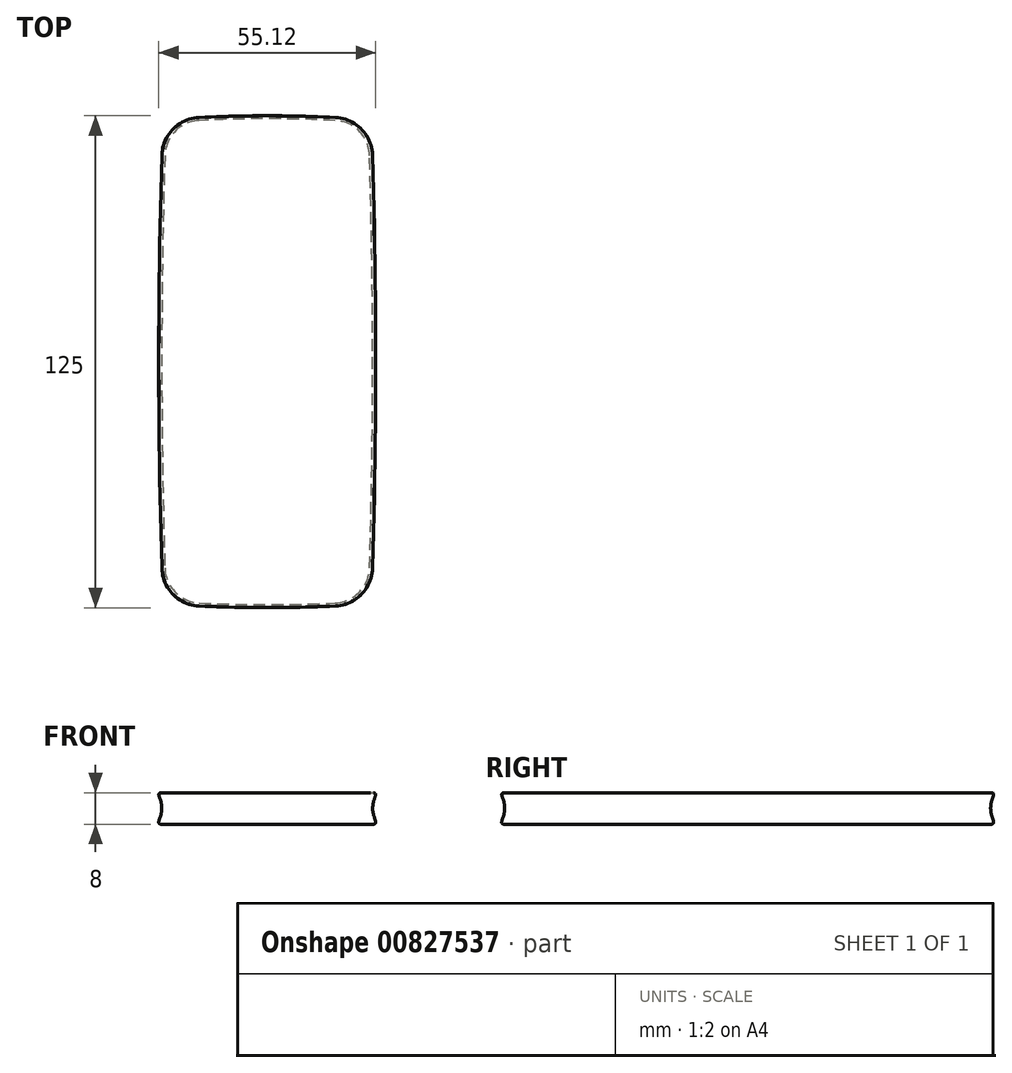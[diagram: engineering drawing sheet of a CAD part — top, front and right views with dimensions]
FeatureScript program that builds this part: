
annotation { "Feature Type Name" : "Feature", "Feature Type Description" : "" }
export const myFeature = defineFeature(function(context is Context, id is Id, definition is map)
    precondition{}
    {
        {
            var Q0;
            Q0=qCreatedBy(makeId("Top.planeOp"),FACE);
            var sketch = newSketch(context, id + "F0", { "sketchPlane" : qUnion([Q0])});
            skPoint(sketch, "E0.middle", {"position": v(0, 0) * mm});
            skArc(sketch, "E1", {"start": v(-26.53, 61.57) * mm, "mid": v(-27.35, 30.8) * mm, "end": v(-27.63, 0) * mm});
            skArc(sketch, "E2", {"start": v(0, 62.56) * mm, "mid": v(-13.28, 62.31) * mm, "end": v(-26.53, 61.57) * mm});
            skPoint(sketch, "E3.orphan", {"position": v(-27.5, 62.5) * mm});
            skArc(sketch, "E4.MirrorCS", {"start": v(-26.53, -61.57) * mm, "mid": v(-27.35, -30.8) * mm, "end": v(-27.63, 0) * mm});
            skArc(sketch, "E5.MirrorCS", {"start": v(0, -62.56) * mm, "mid": v(-13.28, -62.31) * mm, "end": v(-26.53, -61.57) * mm});
            skArc(sketch, "E6.MirrorCS", {"start": v(0, 62.56) * mm, "mid": v(13.28, 62.31) * mm, "end": v(26.53, 61.57) * mm});
            skArc(sketch, "E7.MirrorCS", {"start": v(26.53, 61.57) * mm, "mid": v(27.35, 30.8) * mm, "end": v(27.63, 0) * mm});
            skArc(sketch, "E8.MirrorCS", {"start": v(26.53, -61.57) * mm, "mid": v(27.35, -30.8) * mm, "end": v(27.63, 0) * mm});
            skArc(sketch, "E9.MirrorCS", {"start": v(0, -62.56) * mm, "mid": v(13.28, -62.31) * mm, "end": v(26.53, -61.57) * mm});
            skSolve(sketch);
        }
        {
            var Q0;
            Q0 = qSketchRegion(id + "F0", true);
            extrude(context, id + "F1", {"entities" : qUnion([Q0]), "depth" : 8 * mm, "offsetDistance" : 25 * mm});
        }
        {
            var Q0;
            Q0=makeQuery(id+"F1.opExtrude","SWEPT_EDGE",EDGE,{"disambiguationData":[OSD([sQuery(id+"F0.wireOp",EDGE,"E1"),sQuery(id+"F0.wireOp",EDGE,"E2")])]});
            var Q1;
            Q1=makeQuery(id+"F1.opExtrude","SWEPT_EDGE",EDGE,{"disambiguationData":[OSD([sQuery(id+"F0.wireOp",EDGE,"E6.MirrorCS"),sQuery(id+"F0.wireOp",EDGE,"E7.MirrorCS")])]});
            var Q2;
            Q2=makeQuery(id+"F1.opExtrude","SWEPT_EDGE",EDGE,{"disambiguationData":[OSD([sQuery(id+"F0.wireOp",EDGE,"E4.MirrorCS"),sQuery(id+"F0.wireOp",EDGE,"E5.MirrorCS")])]});
            var Q3;
            Q3=makeQuery(id+"F1.opExtrude","SWEPT_EDGE",EDGE,{"disambiguationData":[OSD([sQuery(id+"F0.wireOp",EDGE,"E8.MirrorCS"),sQuery(id+"F0.wireOp",EDGE,"E9.MirrorCS")])]});
            fillet(context, id + "F2", {"entities" : qUnion([Q0, Q1, Q2, Q3]), "radius" : 10 * mm, "tangentPropagation" : true, "allowEdgeOverflow" : false});
        }
        {
            var Q0;
            Q0=qCreatedBy(makeId("Front.planeOp"),FACE);
            var sketch = newSketch(context, id + "F3", { "sketchPlane" : qUnion([Q0])});
            skCircle(sketch, "E10", {"center": v(-33.74, 4.07) * mm, "radius": 6.95 * mm});
            skPoint(sketch, "E11.start.orphan", {"position": v(-26.8, 4.07) * mm});
            skPoint(sketch, "E12.orphan", {"position": v(-26.8, 8.13) * mm});
            skPoint(sketch, "E13.end.orphan", {"position": v(-26.8, 0) * mm});
            skSolve(sketch);
        }
        {
            var Q0;
            Q0=makeQuery(id+"F1.opExtrude","CAP_FACE",FACE,{"disambiguationData":[OSD([sQuery(id+"F0.wireOp",EDGE,"E1"),sQuery(id+"F0.wireOp",EDGE,"E2"),sQuery(id+"F0.wireOp",EDGE,"E4.MirrorCS"),sQuery(id+"F0.wireOp",EDGE,"E5.MirrorCS"),sQuery(id+"F0.wireOp",EDGE,"E6.MirrorCS"),sQuery(id+"F0.wireOp",EDGE,"E7.MirrorCS"),sQuery(id+"F0.wireOp",EDGE,"E8.MirrorCS"),sQuery(id+"F0.wireOp",EDGE,"E9.MirrorCS")])],"isStart":false});
            cPlane(context, id + "F4", {"entities" : qUnion([Q0]), "cplaneType" : CPlaneType.OFFSET, "offset" : 4 * mm, "oppositeDirection" : true, "width" : 150 * mm, "height" : 150 * mm});
        }
        {
            var Q0;
            Q0=qCreatedBy(id+"F4.planeOp",FACE);
            var sketch = newSketch(context, id + "F5", { "sketchPlane" : qUnion([Q0])});
            skArc(sketch, "E14.0", {"start": v(-25.93, -52.43) * mm, "mid": v(-23.33, -58.53) * mm, "end": v(-17.28, -61.24) * mm});
            skArc(sketch, "E14.1", {"start": v(-25.93, 52.43) * mm, "mid": v(-26.73, 0) * mm, "end": v(-25.93, -52.43) * mm});
            skArc(sketch, "E14.2", {"start": v(-17.28, -61.24) * mm, "mid": v(0, -61.66) * mm, "end": v(17.28, -61.24) * mm});
            skArc(sketch, "E14.3", {"start": v(-17.28, 61.24) * mm, "mid": v(-23.33, 58.53) * mm, "end": v(-25.93, 52.43) * mm});
            skArc(sketch, "E14.4", {"start": v(17.28, -61.24) * mm, "mid": v(23.33, -58.53) * mm, "end": v(25.93, -52.43) * mm});
            skArc(sketch, "E14.5", {"start": v(25.93, -52.43) * mm, "mid": v(26.73, 0) * mm, "end": v(25.93, 52.43) * mm});
            skArc(sketch, "E14.6", {"start": v(25.93, 52.43) * mm, "mid": v(23.33, 58.53) * mm, "end": v(17.28, 61.24) * mm});
            skArc(sketch, "E14.7", {"start": v(17.28, 61.24) * mm, "mid": v(0, 61.66) * mm, "end": v(-17.28, 61.24) * mm});
            skSolve(sketch);
        }
        {
            var Q0;
            Q0=makeQuery(id+"F3.imprint","IMPRINT",FACE,{"disambiguationData":[TD([[makeQuery(id+"F3.imprint","IMPRINT",EDGE,{"derivedFrom":sQuery(id+"F3.wireOp",EDGE,"E10")}),1.0]])]});
            var Q1;
            Q1=sQuery(id+"F5.wireOp",EDGE,"E14.1");
            var Q2;
            Q2=makeQuery(id+"F1.opExtrude","CAP_EDGE",EDGE,{"disambiguationData":[OSD([sQuery(id+"F0.wireOp",EDGE,"E1"),sQuery(id+"F0.wireOp",EDGE,"E4.MirrorCS")])],"isStart":false});
            var Q3;
            {var subQ0=sQuery(id+"F0.wireOp",EDGE,"E5.MirrorCS");var subQ1=sQuery(id+"F0.wireOp",EDGE,"E4.MirrorCS");Q3=makeQuery(id+"F2.opFillet","BLEND_EDGE",EDGE,{"blendedFrom":[makeQuery(id+"F1.opExtrude","SWEPT_EDGE",EDGE,{"disambiguationData":[OSD([subQ1,subQ0])]}),makeQuery(id+"F1.opExtrude","CAP_FACE",FACE,{"disambiguationData":[OSD([sQuery(id+"F0.wireOp",EDGE,"E1"),sQuery(id+"F0.wireOp",EDGE,"E2"),subQ1,subQ0,sQuery(id+"F0.wireOp",EDGE,"E6.MirrorCS"),sQuery(id+"F0.wireOp",EDGE,"E7.MirrorCS"),sQuery(id+"F0.wireOp",EDGE,"E8.MirrorCS"),sQuery(id+"F0.wireOp",EDGE,"E9.MirrorCS")])],"isStart":false})],"blendedInto":[makeQuery(id+"F1.opExtrude","CAP_FACE",FACE,{"disambiguationData":[OSD([sQuery(id+"F0.wireOp",EDGE,"E1"),sQuery(id+"F0.wireOp",EDGE,"E2"),subQ1,subQ0,sQuery(id+"F0.wireOp",EDGE,"E6.MirrorCS"),sQuery(id+"F0.wireOp",EDGE,"E7.MirrorCS"),sQuery(id+"F0.wireOp",EDGE,"E8.MirrorCS"),sQuery(id+"F0.wireOp",EDGE,"E9.MirrorCS")])],"isStart":false})]});}
            var Q4;
            Q4=makeQuery(id+"F1.opExtrude","CAP_EDGE",EDGE,{"disambiguationData":[OSD([sQuery(id+"F0.wireOp",EDGE,"E5.MirrorCS"),sQuery(id+"F0.wireOp",EDGE,"E9.MirrorCS")])],"isStart":false});
            var Q5;
            {var subQ0=sQuery(id+"F0.wireOp",EDGE,"E9.MirrorCS");var subQ1=sQuery(id+"F0.wireOp",EDGE,"E8.MirrorCS");Q5=makeQuery(id+"F2.opFillet","BLEND_EDGE",EDGE,{"blendedFrom":[makeQuery(id+"F1.opExtrude","SWEPT_EDGE",EDGE,{"disambiguationData":[OSD([subQ1,subQ0])]}),makeQuery(id+"F1.opExtrude","CAP_FACE",FACE,{"disambiguationData":[OSD([sQuery(id+"F0.wireOp",EDGE,"E1"),sQuery(id+"F0.wireOp",EDGE,"E2"),sQuery(id+"F0.wireOp",EDGE,"E4.MirrorCS"),sQuery(id+"F0.wireOp",EDGE,"E5.MirrorCS"),sQuery(id+"F0.wireOp",EDGE,"E6.MirrorCS"),sQuery(id+"F0.wireOp",EDGE,"E7.MirrorCS"),subQ1,subQ0])],"isStart":false})],"blendedInto":[makeQuery(id+"F1.opExtrude","CAP_FACE",FACE,{"disambiguationData":[OSD([sQuery(id+"F0.wireOp",EDGE,"E1"),sQuery(id+"F0.wireOp",EDGE,"E2"),sQuery(id+"F0.wireOp",EDGE,"E4.MirrorCS"),sQuery(id+"F0.wireOp",EDGE,"E5.MirrorCS"),sQuery(id+"F0.wireOp",EDGE,"E6.MirrorCS"),sQuery(id+"F0.wireOp",EDGE,"E7.MirrorCS"),subQ1,subQ0])],"isStart":false})]});}
            var Q6;
            Q6=makeQuery(id+"F1.opExtrude","CAP_EDGE",EDGE,{"disambiguationData":[OSD([sQuery(id+"F0.wireOp",EDGE,"E7.MirrorCS"),sQuery(id+"F0.wireOp",EDGE,"E8.MirrorCS")])],"isStart":false});
            var Q7;
            {var subQ0=sQuery(id+"F0.wireOp",EDGE,"E7.MirrorCS");var subQ1=sQuery(id+"F0.wireOp",EDGE,"E6.MirrorCS");Q7=makeQuery(id+"F2.opFillet","BLEND_EDGE",EDGE,{"blendedFrom":[makeQuery(id+"F1.opExtrude","SWEPT_EDGE",EDGE,{"disambiguationData":[OSD([subQ1,subQ0])]}),makeQuery(id+"F1.opExtrude","CAP_FACE",FACE,{"disambiguationData":[OSD([sQuery(id+"F0.wireOp",EDGE,"E1"),sQuery(id+"F0.wireOp",EDGE,"E2"),sQuery(id+"F0.wireOp",EDGE,"E4.MirrorCS"),sQuery(id+"F0.wireOp",EDGE,"E5.MirrorCS"),subQ1,subQ0,sQuery(id+"F0.wireOp",EDGE,"E8.MirrorCS"),sQuery(id+"F0.wireOp",EDGE,"E9.MirrorCS")])],"isStart":false})],"blendedInto":[makeQuery(id+"F1.opExtrude","CAP_FACE",FACE,{"disambiguationData":[OSD([sQuery(id+"F0.wireOp",EDGE,"E1"),sQuery(id+"F0.wireOp",EDGE,"E2"),sQuery(id+"F0.wireOp",EDGE,"E4.MirrorCS"),sQuery(id+"F0.wireOp",EDGE,"E5.MirrorCS"),subQ1,subQ0,sQuery(id+"F0.wireOp",EDGE,"E8.MirrorCS"),sQuery(id+"F0.wireOp",EDGE,"E9.MirrorCS")])],"isStart":false})]});}
            var Q8;
            Q8=makeQuery(id+"F1.opExtrude","CAP_EDGE",EDGE,{"disambiguationData":[OSD([sQuery(id+"F0.wireOp",EDGE,"E2"),sQuery(id+"F0.wireOp",EDGE,"E6.MirrorCS")])],"isStart":false});
            var Q9;
            {var subQ0=sQuery(id+"F0.wireOp",EDGE,"E2");var subQ1=sQuery(id+"F0.wireOp",EDGE,"E1");Q9=makeQuery(id+"F2.opFillet","BLEND_EDGE",EDGE,{"blendedFrom":[makeQuery(id+"F1.opExtrude","SWEPT_EDGE",EDGE,{"disambiguationData":[OSD([subQ1,subQ0])]}),makeQuery(id+"F1.opExtrude","CAP_FACE",FACE,{"disambiguationData":[OSD([subQ1,subQ0,sQuery(id+"F0.wireOp",EDGE,"E4.MirrorCS"),sQuery(id+"F0.wireOp",EDGE,"E5.MirrorCS"),sQuery(id+"F0.wireOp",EDGE,"E6.MirrorCS"),sQuery(id+"F0.wireOp",EDGE,"E7.MirrorCS"),sQuery(id+"F0.wireOp",EDGE,"E8.MirrorCS"),sQuery(id+"F0.wireOp",EDGE,"E9.MirrorCS")])],"isStart":false})],"blendedInto":[makeQuery(id+"F1.opExtrude","CAP_FACE",FACE,{"disambiguationData":[OSD([subQ1,subQ0,sQuery(id+"F0.wireOp",EDGE,"E4.MirrorCS"),sQuery(id+"F0.wireOp",EDGE,"E5.MirrorCS"),sQuery(id+"F0.wireOp",EDGE,"E6.MirrorCS"),sQuery(id+"F0.wireOp",EDGE,"E7.MirrorCS"),sQuery(id+"F0.wireOp",EDGE,"E8.MirrorCS"),sQuery(id+"F0.wireOp",EDGE,"E9.MirrorCS")])],"isStart":false})]});}
            sweep(context, id + "F6", {"operationType" : NewBodyOperationType.REMOVE, "profiles" : qUnion([Q0]), "surfaceProfiles" : qUnion([Q1]), "path" : qUnion([Q2, Q3, Q4, Q5, Q6, Q7, Q8, Q9])});
        }
        {
            var Q0;
            {var subQ0=sQuery(id+"F3.wireOp",EDGE,"E10");var subQ1=sQuery(id+"F0.wireOp",EDGE,"E9.MirrorCS");var subQ2=sQuery(id+"F0.wireOp",EDGE,"E8.MirrorCS");var subQ3=sQuery(id+"F0.wireOp",EDGE,"E7.MirrorCS");var subQ4=sQuery(id+"F0.wireOp",EDGE,"E6.MirrorCS");var subQ5=sQuery(id+"F0.wireOp",EDGE,"E5.MirrorCS");var subQ6=sQuery(id+"F0.wireOp",EDGE,"E4.MirrorCS");var subQ7=sQuery(id+"F0.wireOp",EDGE,"E2");var subQ8=sQuery(id+"F0.wireOp",EDGE,"E1");Q0=makeQuery(id+"F6.boolean.opBoolean","INTERSECT",EDGE,{"disambiguationData":[OD(0.0)],"derivedFrom":[makeQuery(id+"F2.opFillet","BLEND_FACE",FACE,{"disambiguationData":[OSD([subQ8,subQ7])]}),makeQuery(id+"F6.opSweep","SWEPT_FACE",FACE,{"disambiguationData":[OSD([subQ8,subQ7,subQ6,subQ5,subQ4,subQ3,subQ2,subQ1,subQ0]),TDD([makeQuery(id+"F2.opFillet","BLEND_EDGE",EDGE,{"blendedFrom":[makeQuery(id+"F1.opExtrude","SWEPT_EDGE",EDGE,{"disambiguationData":[OSD([subQ8,subQ7])]}),makeQuery(id+"F1.opExtrude","CAP_FACE",FACE,{"disambiguationData":[OSD([subQ8,subQ7,subQ6,subQ5,subQ4,subQ3,subQ2,subQ1])],"isStart":false})],"blendedInto":[makeQuery(id+"F1.opExtrude","CAP_FACE",FACE,{"disambiguationData":[OSD([subQ8,subQ7,subQ6,subQ5,subQ4,subQ3,subQ2,subQ1])],"isStart":false})]}),makeQuery(id+"F3.imprint","IMPRINT",EDGE,{"derivedFrom":subQ0})])]})]});}
            var Q1;
            {var subQ0=sQuery(id+"F3.wireOp",EDGE,"E10");var subQ1=sQuery(id+"F0.wireOp",EDGE,"E9.MirrorCS");var subQ2=sQuery(id+"F0.wireOp",EDGE,"E8.MirrorCS");var subQ3=sQuery(id+"F0.wireOp",EDGE,"E7.MirrorCS");var subQ4=sQuery(id+"F0.wireOp",EDGE,"E6.MirrorCS");var subQ5=sQuery(id+"F0.wireOp",EDGE,"E5.MirrorCS");var subQ6=sQuery(id+"F0.wireOp",EDGE,"E4.MirrorCS");var subQ7=sQuery(id+"F0.wireOp",EDGE,"E2");var subQ8=sQuery(id+"F0.wireOp",EDGE,"E1");Q1=makeQuery(id+"F6.boolean.opBoolean","INTERSECT",EDGE,{"disambiguationData":[OD(1.0)],"derivedFrom":[makeQuery(id+"F2.opFillet","BLEND_FACE",FACE,{"disambiguationData":[OSD([subQ8,subQ7])]}),makeQuery(id+"F6.opSweep","SWEPT_FACE",FACE,{"disambiguationData":[OSD([subQ8,subQ7,subQ6,subQ5,subQ4,subQ3,subQ2,subQ1,subQ0]),TDD([makeQuery(id+"F2.opFillet","BLEND_EDGE",EDGE,{"blendedFrom":[makeQuery(id+"F1.opExtrude","SWEPT_EDGE",EDGE,{"disambiguationData":[OSD([subQ8,subQ7])]}),makeQuery(id+"F1.opExtrude","CAP_FACE",FACE,{"disambiguationData":[OSD([subQ8,subQ7,subQ6,subQ5,subQ4,subQ3,subQ2,subQ1])],"isStart":false})],"blendedInto":[makeQuery(id+"F1.opExtrude","CAP_FACE",FACE,{"disambiguationData":[OSD([subQ8,subQ7,subQ6,subQ5,subQ4,subQ3,subQ2,subQ1])],"isStart":false})]}),makeQuery(id+"F3.imprint","IMPRINT",EDGE,{"derivedFrom":subQ0})])]})]});}
            fillet(context, id + "F7", {"entities" : qUnion([Q0, Q1]), "radius" : 5 * mm, "tangentPropagation" : true, "allowEdgeOverflow" : false});
        }
        {
            var Q0;
            {var subQ0=sQuery(id+"F0.wireOp",EDGE,"E9.MirrorCS");var subQ1=sQuery(id+"F0.wireOp",EDGE,"E5.MirrorCS");Q0=makeQuery(id+"F7.opFillet","BLEND_EDGE",EDGE,{"blendedFrom":[makeQuery(id+"F6.boolean.opBoolean","INTERSECT",EDGE,{"disambiguationData":[OD(0.0)],"derivedFrom":[makeQuery(id+"F1.opExtrude","SWEPT_FACE",FACE,{"disambiguationData":[OSD([subQ1,subQ0])]}),makeQuery(id+"F6.opSweep","SWEPT_FACE",FACE,{"disambiguationData":[OSD([subQ1,subQ0,sQuery(id+"F3.wireOp",EDGE,"E10")])]})]}),makeQuery(id+"F1.opExtrude","CAP_FACE",FACE,{"disambiguationData":[OSD([sQuery(id+"F0.wireOp",EDGE,"E1"),sQuery(id+"F0.wireOp",EDGE,"E2"),sQuery(id+"F0.wireOp",EDGE,"E4.MirrorCS"),subQ1,sQuery(id+"F0.wireOp",EDGE,"E6.MirrorCS"),sQuery(id+"F0.wireOp",EDGE,"E7.MirrorCS"),sQuery(id+"F0.wireOp",EDGE,"E8.MirrorCS"),subQ0])],"isStart":true})],"blendedInto":[makeQuery(id+"F1.opExtrude","CAP_FACE",FACE,{"disambiguationData":[OSD([sQuery(id+"F0.wireOp",EDGE,"E1"),sQuery(id+"F0.wireOp",EDGE,"E2"),sQuery(id+"F0.wireOp",EDGE,"E4.MirrorCS"),subQ1,sQuery(id+"F0.wireOp",EDGE,"E6.MirrorCS"),sQuery(id+"F0.wireOp",EDGE,"E7.MirrorCS"),sQuery(id+"F0.wireOp",EDGE,"E8.MirrorCS"),subQ0])],"isStart":true})]});}
            var Q1;
            {var subQ0=sQuery(id+"F0.wireOp",EDGE,"E9.MirrorCS");var subQ1=sQuery(id+"F0.wireOp",EDGE,"E8.MirrorCS");var subQ2=sQuery(id+"F0.wireOp",EDGE,"E7.MirrorCS");var subQ3=sQuery(id+"F0.wireOp",EDGE,"E6.MirrorCS");var subQ4=sQuery(id+"F0.wireOp",EDGE,"E5.MirrorCS");var subQ5=sQuery(id+"F0.wireOp",EDGE,"E4.MirrorCS");var subQ6=sQuery(id+"F0.wireOp",EDGE,"E2");var subQ7=sQuery(id+"F0.wireOp",EDGE,"E1");var subQ8=makeQuery(id+"F1.opExtrude","CAP_FACE",FACE,{"disambiguationData":[OSD([subQ7,subQ6,subQ5,subQ4,subQ3,subQ2,subQ1,subQ0])],"isStart":false});var subQ9=sQuery(id+"F3.wireOp",EDGE,"E10");Q1=makeQuery(id+"F7.opFillet","BLEND_EDGE",EDGE,{"blendedFrom":[makeQuery(id+"F6.boolean.opBoolean","INTERSECT",EDGE,{"disambiguationData":[OD(1.0)],"derivedFrom":[makeQuery(id+"F2.opFillet","BLEND_FACE",FACE,{"disambiguationData":[OSD([subQ5,subQ4])]}),makeQuery(id+"F6.opSweep","SWEPT_FACE",FACE,{"disambiguationData":[OSD([subQ7,subQ6,subQ5,subQ4,subQ3,subQ2,subQ1,subQ0,subQ9]),TDD([makeQuery(id+"F2.opFillet","BLEND_EDGE",EDGE,{"blendedFrom":[makeQuery(id+"F1.opExtrude","SWEPT_EDGE",EDGE,{"disambiguationData":[OSD([subQ5,subQ4])]}),subQ8],"blendedInto":[subQ8]}),makeQuery(id+"F3.imprint","IMPRINT",EDGE,{"derivedFrom":subQ9})])]})]}),subQ8],"blendedInto":[subQ8]});}
            fillet(context, id + "F8", {"entities" : qUnion([Q0, Q1]), "radius" : 0.5 * mm, "tangentPropagation" : true, "allowEdgeOverflow" : false});
        }
    });
